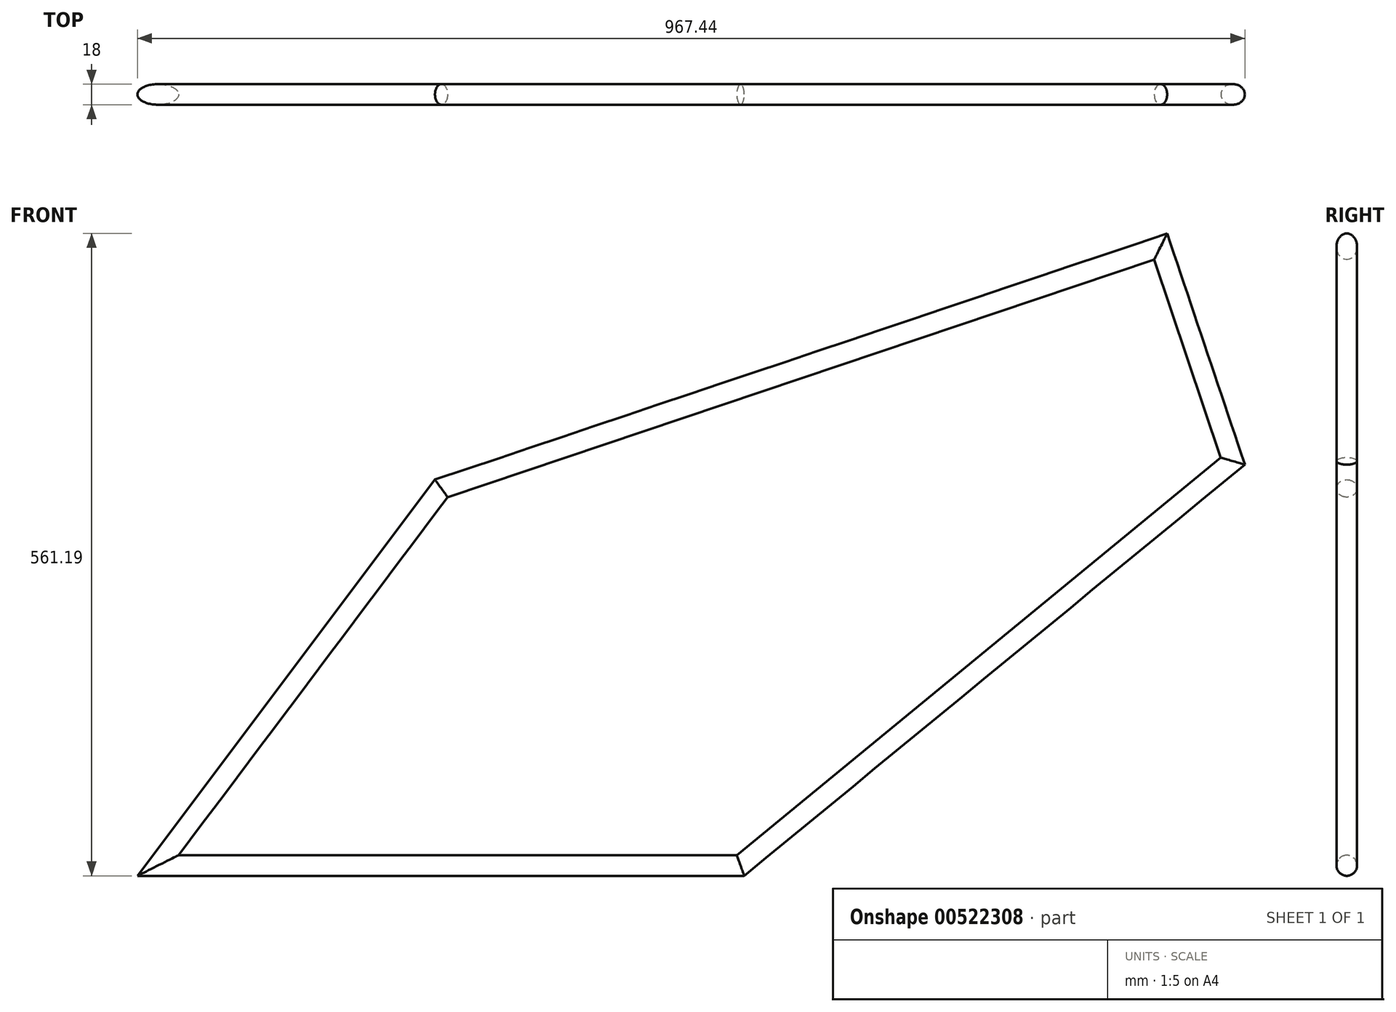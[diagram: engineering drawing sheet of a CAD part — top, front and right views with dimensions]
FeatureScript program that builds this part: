
annotation { "Feature Type Name" : "Feature", "Feature Type Description" : "" }
export const myFeature = defineFeature(function(context is Context, id is Id, definition is map)
    precondition{}
    {
        {
            var Q0;
            Q0=qCreatedBy(makeId("Front.planeOp"),FACE);
            var sketch = newSketch(context, id + "F0", { "sketchPlane" : qUnion([Q0])});
            skLineSegment(sketch, "E0", {"start": v(0, 0) * mm, "end": v(247.46, 329.47) * mm});
            skLineSegment(sketch, "E1", {"start": v(247.46, 329.47) * mm, "end": v(875.85, 540.79) * mm});
            skLineSegment(sketch, "E2", {"start": v(875.85, 540.79) * mm, "end": v(938.9, 353.28) * mm});
            skLineSegment(sketch, "E3", {"start": v(938.9, 353.28) * mm, "end": v(508.83, 0) * mm});
            skLineSegment(sketch, "E4", {"start": v(508.83, 0) * mm, "end": v(0, 0) * mm});
            skLineSegment(sketch, "E5", {"start": v(903.66, 557.47) * mm, "end": v(992.63, 296.1) * mm});
            skLineSegment(sketch, "E6", {"start": v(992.63, 296.1) * mm, "end": v(1140, 0) * mm});
            skSolve(sketch);
        }
        {
            var Q0;
            Q0=qCreatedBy(makeId("Right.planeOp"),FACE);
            var sketch = newSketch(context, id + "F1", { "sketchPlane" : qUnion([Q0])});
            skCircle(sketch, "E7", {"center": v(0, 0) * mm, "radius": 9 * mm});
            skSolve(sketch);
        }
        {
            var Q0;
            Q0=makeQuery(id+"F1.imprint","IMPRINT",FACE,{"disambiguationData":[TD([[makeQuery(id+"F1.imprint","IMPRINT",EDGE,{"derivedFrom":sQuery(id+"F1.wireOp",EDGE,"E7")}),1.0]])]});
            var Q1;
            Q1=sQuery(id+"F0.wireOp",EDGE,"E4");
            var Q2;
            Q2=sQuery(id+"F0.wireOp",EDGE,"E3");
            var Q3;
            Q3=sQuery(id+"F0.wireOp",EDGE,"E2");
            var Q4;
            Q4=sQuery(id+"F0.wireOp",EDGE,"E1");
            var Q5;
            Q5=sQuery(id+"F0.wireOp",EDGE,"E0");
            sweep(context, id + "F2", {"profiles" : qUnion([Q0]), "path" : qUnion([Q1, Q2, Q3, Q4, Q5])});
        }
    });
